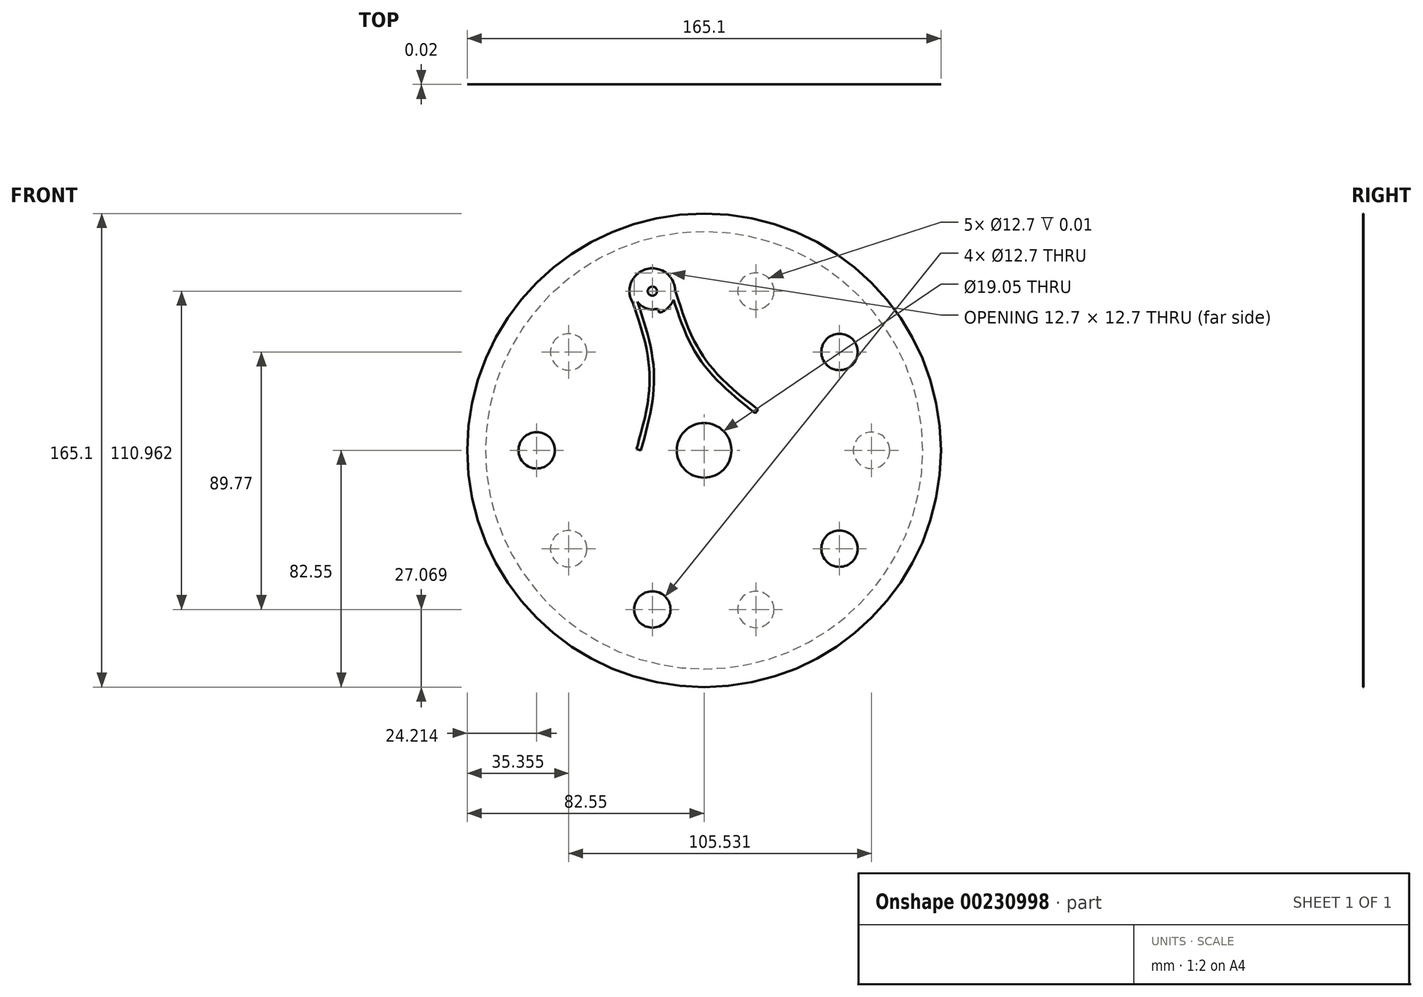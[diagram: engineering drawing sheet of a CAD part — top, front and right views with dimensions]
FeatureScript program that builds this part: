
annotation { "Feature Type Name" : "Feature", "Feature Type Description" : "" }
export const myFeature = defineFeature(function(context is Context, id is Id, definition is map)
    precondition{}
    {
        {
            var Q0;
            Q0=qCreatedBy(makeId("Front.planeOp"),FACE);
            var sketch = newSketch(context, id + "F0", { "sketchPlane" : qUnion([Q0])});
            skCircle(sketch, "E0", {"center": v(0, 0) * mm, "radius": 76.2 * mm});
            skCircle(sketch, "E1", {"center": v(0, 0) * mm, "radius": 9.53 * mm});
            skCircle(sketch, "E2", {"center": v(58.34, 0) * mm, "radius": 6.35 * mm});
            skCircle(sketch, "E3.1.0", {"center": v(47.2, -34.29) * mm, "radius": 6.35 * mm});
            skCircle(sketch, "E3.2.0", {"center": v(18.03, -55.48) * mm, "radius": 6.35 * mm});
            skCircle(sketch, "E3.3.0", {"center": v(-18.03, -55.48) * mm, "radius": 6.35 * mm});
            skCircle(sketch, "E3.4.0", {"center": v(-47.2, -34.29) * mm, "radius": 6.35 * mm});
            skCircle(sketch, "E3.5.0", {"center": v(-58.34, 0) * mm, "radius": 6.35 * mm});
            skCircle(sketch, "E3.6.0", {"center": v(-47.2, 34.29) * mm, "radius": 6.35 * mm});
            skCircle(sketch, "E3.7.0", {"center": v(-18.03, 55.48) * mm, "radius": 6.35 * mm});
            skCircle(sketch, "E3.8.0", {"center": v(18.03, 55.48) * mm, "radius": 6.35 * mm});
            skCircle(sketch, "E3.9.0", {"center": v(47.2, 34.29) * mm, "radius": 6.35 * mm});
            skLineSegment(sketch, "E3.anchor1", {"start": v(0, 0) * mm, "end": v(58.34, 0) * mm, "construction": true});
            skLineSegment(sketch, "E3.anchor2", {"start": v(0, 0) * mm, "end": v(47.2, 34.29) * mm, "construction": true});
            skSolve(sketch);
        }
        {
            var Q0;
            Q0=makeQuery(id+"F0.imprint","IMPRINT",FACE,{"disambiguationData":[TD([[makeQuery(id+"F0.imprint","IMPRINT",EDGE,{"derivedFrom":sQuery(id+"F0.wireOp",EDGE,"E0")}),1.0]])]});
            extrude(context, id + "F1", {"entities" : qUnion([Q0]), "depth" : 1 / 101.6 * mm});
        }
        {
            var Q0;
            Q0=makeQuery(id+"F1.opExtrude","CAP_FACE",FACE,{"disambiguationData":[OSD([sQuery(id+"F0.wireOp",EDGE,"E0"),sQuery(id+"F0.wireOp",EDGE,"E1"),sQuery(id+"F0.wireOp",EDGE,"E2"),sQuery(id+"F0.wireOp",EDGE,"E3.1.0"),sQuery(id+"F0.wireOp",EDGE,"E3.2.0"),sQuery(id+"F0.wireOp",EDGE,"E3.3.0"),sQuery(id+"F0.wireOp",EDGE,"E3.4.0"),sQuery(id+"F0.wireOp",EDGE,"E3.5.0"),sQuery(id+"F0.wireOp",EDGE,"E3.6.0"),sQuery(id+"F0.wireOp",EDGE,"E3.7.0"),sQuery(id+"F0.wireOp",EDGE,"E3.8.0"),sQuery(id+"F0.wireOp",EDGE,"E3.9.0")])],"isStart":false});
            var sketch = newSketch(context, id + "F2", { "sketchPlane" : qUnion([Q0])});
            skCircle(sketch, "E4", {"center": v(0, 0) * mm, "radius": 82.55 * mm});
            skCircle(sketch, "E5", {"center": v(-18.03, 55.48) * mm, "radius": 6.37 * mm});
            skFitSpline(sketch, "E6", {"points": [v(-23.27, 51.9) * mm, v(-17.44, 26.26) * mm, v(-22, 0) * mm], "startDerivative": vector(16.88, -51.22) * mm, "endDerivative": vector(-14.32, -52.56) * mm});
            skLineSegment(sketch, "E7", {"start": v(-18.03, 55.48) * mm, "end": v(0, 0) * mm});
            skFitSpline(sketch, "E8.MirrorCS", {"points": [v(-11.68, 55.66) * mm, v(-1.33, 31.5) * mm, v(17.8, 12.93) * mm], "startDerivative": vector(16.45, -51.36) * mm, "endDerivative": vector(42.48, -34.1) * mm});
            skFitSpline(sketch, "E9.0", {"points": [v(-10.17, 56.14) * mm, v(-9.48, 54) * mm, v(-8.12, 49.74) * mm, v(-5.88, 43.54) * mm, v(-3.7, 38.64) * mm, v(-1.68, 34.94) * mm, v(0, 32.3) * mm, v(1.87, 29.8) * mm, v(4.62, 26.57) * mm, v(8.46, 22.77) * mm, v(13.5, 18.42) * mm, v(17.03, 15.6) * mm, v(18.8, 14.17) * mm]});
            skCircle(sketch, "E10.0", {"center": v(-18.03, 55.48) * mm, "radius": 7.96 * mm});
            skFitSpline(sketch, "E11.0", {"points": [v(-24.77, 51.4) * mm, v(-24.07, 49.26) * mm, v(-22.67, 45.01) * mm, v(-20.83, 38.68) * mm, v(-19.7, 33.44) * mm, v(-19.18, 29.26) * mm, v(-18.98, 26.13) * mm, v(-19.03, 23) * mm, v(-19.36, 18.78) * mm, v(-20.22, 13.45) * mm, v(-21.75, 6.97) * mm, v(-22.94, 2.6) * mm, v(-23.54, 0.42) * mm]});
            skLineSegment(sketch, "E12", {"start": v(17.8, 12.93) * mm, "end": v(18.8, 14.17) * mm});
            skLineSegment(sketch, "E13", {"start": v(-22, 0) * mm, "end": v(-23.54, 0.42) * mm});
            skCircle(sketch, "E14", {"center": v(-18.03, 55.48) * mm, "radius": 1.59 * mm});
            skCircle(sketch, "E15", {"center": v(0, 0) * mm, "radius": 6.35 * mm});
            skSolve(sketch);
        }
        {
            var Q0;
            {var subQ0=sQuery(id+"F2.wireOp",EDGE,"E12");Q0=makeQuery(id+"F2.imprint","IMPRINT",FACE,{"disambiguationData":[TD([[makeQuery(id+"F2.imprint","IMPRINT",EDGE,{"derivedFrom":subQ0}),-1.0]])]});}
            var Q1;
            Q1=makeQuery(id+"F2.imprint","IMPRINT",FACE,{"disambiguationData":[TD([[makeQuery(id+"F2.imprint","IMPRINT",EDGE,{"derivedFrom":sQuery(id+"F2.wireOp",EDGE,"E4")}),1.0]])]});
            var Q2;
            Q2=makeQuery(id+"F2.imprint","IMPRINT",FACE,{"disambiguationData":[TD([[makeQuery(id+"F2.imprint","IMPRINT",EDGE,{"derivedFrom":makeQuery(id+"F1.opExtrude","CAP_EDGE",EDGE,{"disambiguationData":[OSD([sQuery(id+"F0.wireOp",EDGE,"E3.8.0")])],"isStart":false})}),1.0]])]});
            var Q3;
            Q3=makeQuery(id+"F2.imprint","IMPRINT",FACE,{"disambiguationData":[TD([[makeQuery(id+"F2.imprint","IMPRINT",EDGE,{"derivedFrom":makeQuery(id+"F1.opExtrude","CAP_EDGE",EDGE,{"disambiguationData":[OSD([sQuery(id+"F0.wireOp",EDGE,"E2")])],"isStart":false})}),1.0]])]});
            var Q4;
            Q4=makeQuery(id+"F2.imprint","IMPRINT",FACE,{"disambiguationData":[TD([[makeQuery(id+"F2.imprint","IMPRINT",EDGE,{"derivedFrom":makeQuery(id+"F1.opExtrude","CAP_EDGE",EDGE,{"disambiguationData":[OSD([sQuery(id+"F0.wireOp",EDGE,"E3.2.0")])],"isStart":false})}),1.0]])]});
            var Q5;
            Q5=makeQuery(id+"F2.imprint","IMPRINT",FACE,{"disambiguationData":[TD([[makeQuery(id+"F2.imprint","IMPRINT",EDGE,{"derivedFrom":makeQuery(id+"F1.opExtrude","CAP_EDGE",EDGE,{"disambiguationData":[OSD([sQuery(id+"F0.wireOp",EDGE,"E3.4.0")])],"isStart":false})}),1.0]])]});
            var Q6;
            Q6=makeQuery(id+"F2.imprint","IMPRINT",FACE,{"disambiguationData":[TD([[makeQuery(id+"F2.imprint","IMPRINT",EDGE,{"derivedFrom":makeQuery(id+"F1.opExtrude","CAP_EDGE",EDGE,{"disambiguationData":[OSD([sQuery(id+"F0.wireOp",EDGE,"E3.6.0")])],"isStart":false})}),1.0]])]});
            var Q7;
            Q7=makeQuery(id+"F2.imprint","IMPRINT",FACE,{"disambiguationData":[TD([[makeQuery(id+"F2.imprint","IMPRINT",EDGE,{"derivedFrom":sQuery(id+"F2.wireOp",EDGE,"E14")}),-1.0]])]});
            var Q8;
            {var subQ0=sQuery(id+"F2.wireOp",EDGE,"E6");var subQ1=sQuery(id+"F2.wireOp",EDGE,"E5");var subQ2=makeQuery(id+"F2.imprint","INTERSECT",VERTEX,{"derivedFrom":[subQ1,subQ0]});Q8=makeQuery(id+"F2.imprint","IMPRINT",FACE,{"disambiguationData":[TD([[makeQuery(id+"F2.imprint","IMPRINT",EDGE,{"disambiguationData":[TD([[subQ2,-1.0]])],"derivedFrom":subQ1}),-1.0]])]});}
            extrude(context, id + "F3", {"entities" : qUnion([Q0, Q1, Q2, Q3, Q4, Q5, Q6, Q7, Q8]), "operationType" : NewBodyOperationType.ADD, "depth" : 1 / 101.6 * mm});
        }
    });
